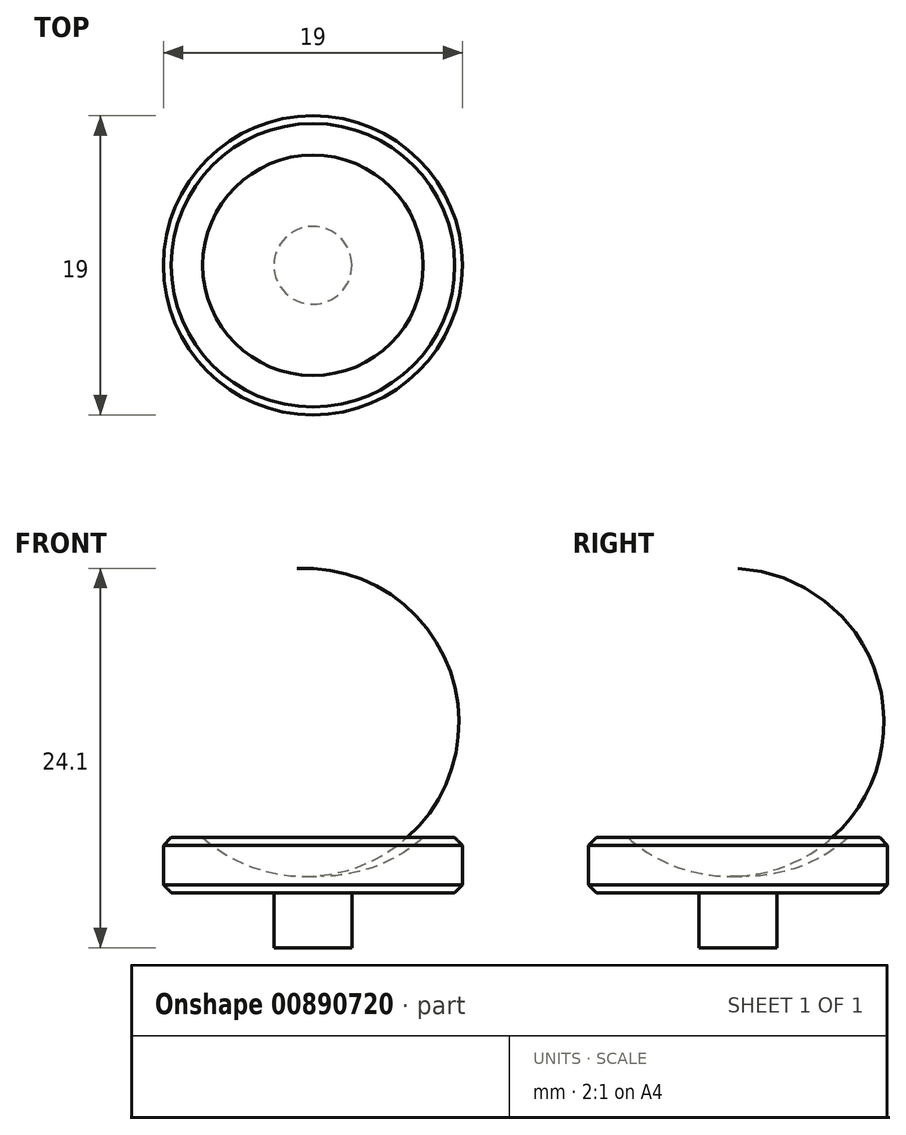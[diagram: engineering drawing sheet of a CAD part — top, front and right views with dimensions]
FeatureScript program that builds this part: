
annotation { "Feature Type Name" : "Feature", "Feature Type Description" : "" }
export const myFeature = defineFeature(function(context is Context, id is Id, definition is map)
    precondition{}
    {
        {
            var Q0;
            Q0=qCreatedBy(makeId("Front.planeOp"),FACE);
            var sketch = newSketch(context, id + "F0", { "sketchPlane" : qUnion([Q0])});
            skLineSegment(sketch, "E0", {"start": v(0, 0) * mm, "end": v(2.48, 0) * mm});
            skLineSegment(sketch, "E1", {"start": v(2.48, 0) * mm, "end": v(2.48, 3.5) * mm});
            skLineSegment(sketch, "E2", {"start": v(2.47, 3.5) * mm, "end": v(9.5, 3.5) * mm});
            skLineSegment(sketch, "E3", {"start": v(9.5, 3.5) * mm, "end": v(9.5, 7) * mm});
            skLineSegment(sketch, "E4", {"start": v(9.5, 7) * mm, "end": v(7, 7) * mm});
            skPoint(sketch, "E5", {"position": v(0, 4.55) * mm});
            skLineSegment(sketch, "E6", {"start": v(0, 0) * mm, "end": v(0, 4.55) * mm});
            skArc(sketch, "E7", {"start": v(0, 4.55) * mm, "mid": v(3.74, 5.09) * mm, "end": v(7, 7) * mm});
            skSolve(sketch);
        }
        {
            var Q0;
            Q0=makeQuery(id+"F0.imprint","IMPRINT",FACE,{"disambiguationData":[TD([[makeQuery(id+"F0.imprint","IMPRINT",EDGE,{"derivedFrom":sQuery(id+"F0.wireOp",EDGE,"E0")}),1.0]])]});
            var Q1;
            Q1=sQuery(id+"F0.wireOp",EDGE,"E6");
            revolve(context, id + "F1", {"surfaceOperationType" : NewSurfaceOperationType.NEW, "entities" : qUnion([Q0]), "axis" : qUnion([Q1]), "revolveType" : RevolveType.FULL});
        }
        {
            var Q0;
            Q0=makeQuery(id+"F1.opRevolve","SWEPT_EDGE",EDGE,{"disambiguationData":[OSD([sQuery(id+"F0.wireOp",EDGE,"E3"),sQuery(id+"F0.wireOp",EDGE,"E4")])]});
            var Q1;
            Q1=makeQuery(id+"F1.opRevolve","SWEPT_EDGE",EDGE,{"disambiguationData":[OSD([sQuery(id+"F0.wireOp",EDGE,"E2"),sQuery(id+"F0.wireOp",EDGE,"E3")])]});
            chamfer(context, id + "F2", {"entities" : qUnion([Q0, Q1]), "width" : 0.5 * mm, "tangentPropagation" : true});
        }
    });
